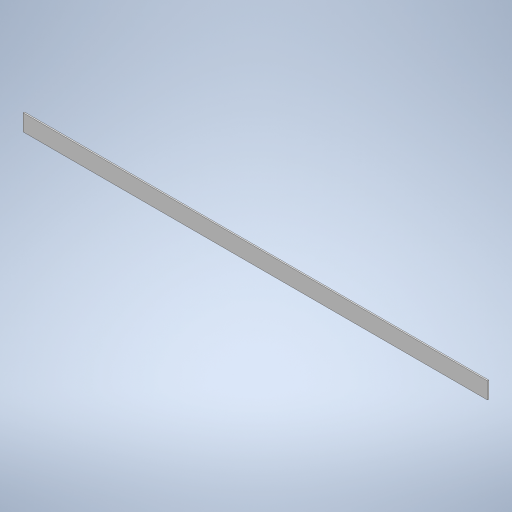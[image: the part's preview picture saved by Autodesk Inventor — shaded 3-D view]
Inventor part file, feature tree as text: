
AUTODESK INVENTOR PART (.ipt)
format: ipt  version: 2023.1 (Build 271208000, 208)  size: 241,152 bytes
history: native  units: mm
features: sheet_metal_op x1, sketch x1, other x1
ambient origin geometry x8: Origin, YZ Plane, XZ Plane, XY Plane, X Axis, Y Axis, Z Axis, Center Point
bodies: Solid1 (feature_tree)
feature tree (3):
  sheet_metal_op  "Face1"
  sketch  "Sketch1"  dims[d0=700.0mm d1=25.0mm d2=2.0mm]
  other  "Plate1"
